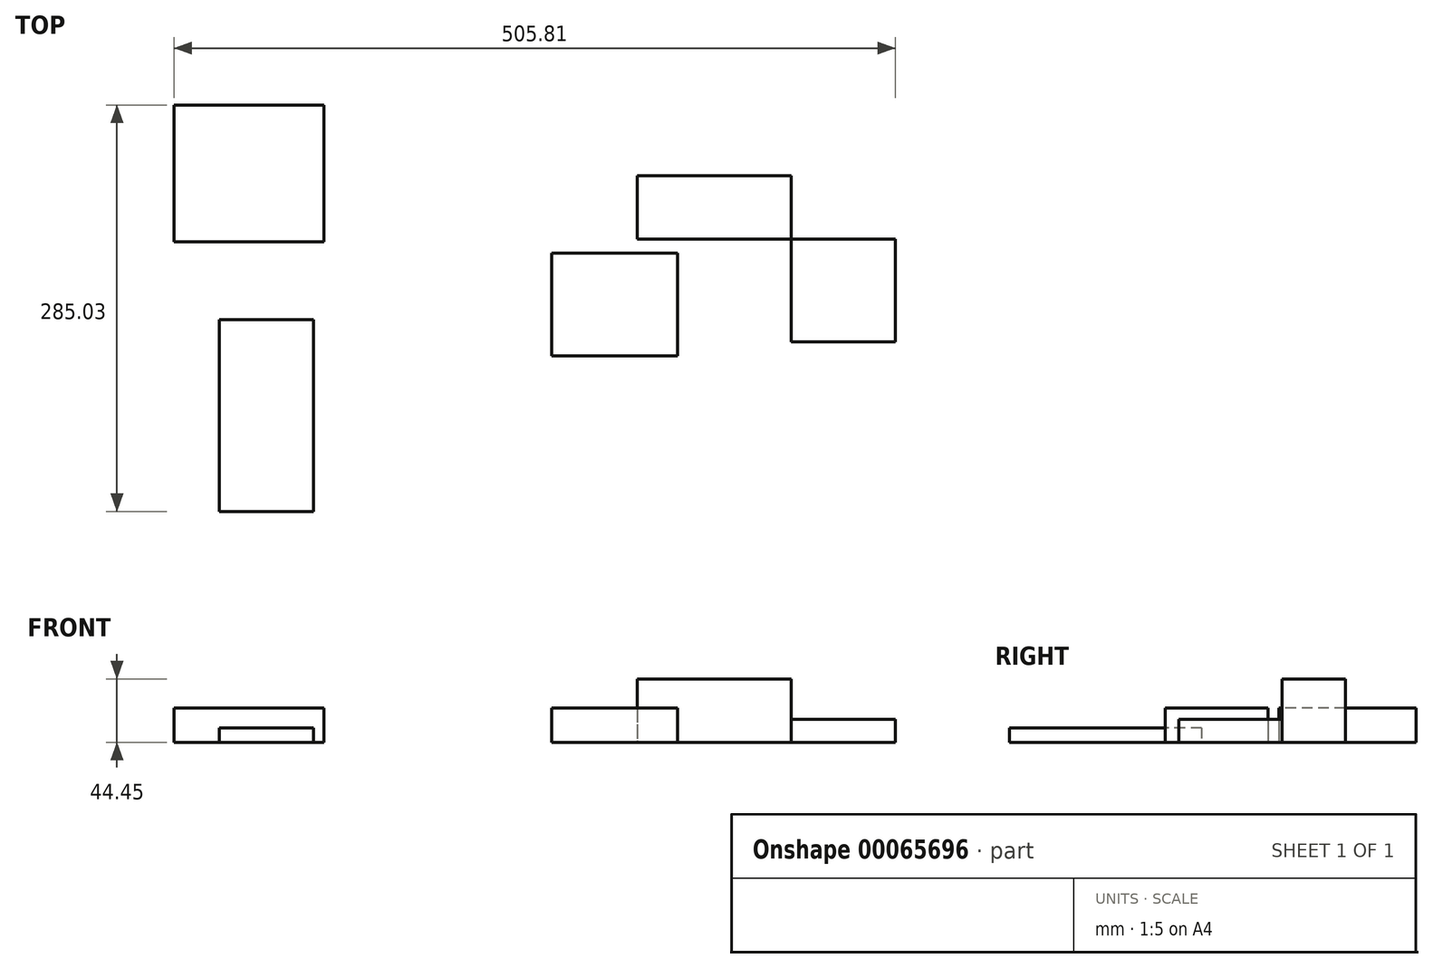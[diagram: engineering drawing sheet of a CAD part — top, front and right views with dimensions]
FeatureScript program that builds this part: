
annotation { "Feature Type Name" : "Feature", "Feature Type Description" : "" }
export const myFeature = defineFeature(function(context is Context, id is Id, definition is map)
    precondition{}
    {
        {
            var Q0;
            Q0=qCreatedBy(makeId("Top.planeOp"),FACE);
            var sketch = newSketch(context, id + "F0", { "sketchPlane" : qUnion([Q0])});
            skLineSegment(sketch, "E0.bottom", {"start": v(-107.95, 44.45) * mm, "end": v(0, 44.45) * mm});
            skLineSegment(sketch, "E0.top", {"start": v(-107.95, 0) * mm, "end": v(0, 0) * mm});
            skLineSegment(sketch, "E0.left", {"start": v(-107.95, 44.45) * mm, "end": v(-107.95, 0) * mm});
            skLineSegment(sketch, "E0.right", {"start": v(0, 44.45) * mm, "end": v(0, 0) * mm});
            skSolve(sketch);
        }
        {
            var Q0;
            Q0=makeQuery(id+"F0.imprint","IMPRINT",FACE,{"disambiguationData":[TD([[makeQuery(id+"F0.imprint","IMPRINT",EDGE,{"derivedFrom":sQuery(id+"F0.wireOp",EDGE,"E0.bottom")}),-1.0]])]});
            extrude(context, id + "F1", {"entities" : qUnion([Q0]), "depth" : 44.45 * mm});
        }
        {
            var Q0;
            Q0=qCreatedBy(makeId("Top.planeOp"),FACE);
            var sketch = newSketch(context, id + "F2", { "sketchPlane" : qUnion([Q0])});
            skLineSegment(sketch, "E1.bottom", {"start": v(0, 0) * mm, "end": v(73.15, 0) * mm});
            skLineSegment(sketch, "E1.top", {"start": v(0, -72.14) * mm, "end": v(73.15, -72.14) * mm});
            skLineSegment(sketch, "E1.left", {"start": v(0, 0) * mm, "end": v(0, -72.14) * mm});
            skLineSegment(sketch, "E1.right", {"start": v(73.15, 0) * mm, "end": v(73.15, -72.14) * mm});
            skSolve(sketch);
        }
        {
            var Q0;
            Q0=makeQuery(id+"F2.imprint","IMPRINT",FACE,{"disambiguationData":[TD([[makeQuery(id+"F2.imprint","IMPRINT",EDGE,{"derivedFrom":sQuery(id+"F2.wireOp",EDGE,"E1.bottom")}),-1.0]])]});
            extrude(context, id + "F3", {"entities" : qUnion([Q0]), "depth" : 16.26 * mm});
        }
        {
            var Q0;
            Q0=qCreatedBy(makeId("Top.planeOp"),FACE);
            var sketch = newSketch(context, id + "F4", { "sketchPlane" : qUnion([Q0])});
            skLineSegment(sketch, "E2.bottom", {"start": v(-167.83, -9.68) * mm, "end": v(-79.69, -9.68) * mm});
            skLineSegment(sketch, "E2.top", {"start": v(-167.83, -81.82) * mm, "end": v(-79.69, -81.82) * mm});
            skLineSegment(sketch, "E2.left", {"start": v(-167.83, -9.68) * mm, "end": v(-167.83, -81.82) * mm});
            skLineSegment(sketch, "E2.right", {"start": v(-79.69, -9.68) * mm, "end": v(-79.69, -81.82) * mm});
            skSolve(sketch);
        }
        {
            var Q0;
            Q0=qSketchRegion(id+"F4",true);
            extrude(context, id + "F5", {"entities" : qUnion([Q0]), "depth" : 24.13 * mm});
        }
        {
            var Q0;
            Q0=qCreatedBy(makeId("Top.planeOp"),FACE);
            var sketch = newSketch(context, id + "F6", { "sketchPlane" : qUnion([Q0])});
            skLineSegment(sketch, "E3.bottom", {"start": v(-432.66, 94.04) * mm, "end": v(-327.5, 94.04) * mm});
            skLineSegment(sketch, "E3.top", {"start": v(-432.66, -1.97) * mm, "end": v(-327.5, -1.97) * mm});
            skLineSegment(sketch, "E3.left", {"start": v(-432.66, 94.04) * mm, "end": v(-432.66, -1.97) * mm});
            skLineSegment(sketch, "E3.right", {"start": v(-327.5, 94.04) * mm, "end": v(-327.5, -1.97) * mm});
            skSolve(sketch);
        }
        {
            var Q0;
            Q0=makeQuery(id+"F6.imprint","IMPRINT",FACE,{"disambiguationData":[TD([[makeQuery(id+"F6.imprint","IMPRINT",EDGE,{"derivedFrom":sQuery(id+"F6.wireOp",EDGE,"E3.bottom")}),-1.0]])]});
            extrude(context, id + "F7", {"entities" : qUnion([Q0]), "depth" : 24.13 * mm});
        }
        {
            var Q0;
            Q0=qCreatedBy(makeId("Top.planeOp"),FACE);
            var sketch = newSketch(context, id + "F8", { "sketchPlane" : qUnion([Q0])});
            skLineSegment(sketch, "E4.bottom", {"start": v(-401.06, -56.37) * mm, "end": v(-335.02, -56.37) * mm});
            skLineSegment(sketch, "E4.top", {"start": v(-401.06, -191) * mm, "end": v(-335.02, -191) * mm});
            skLineSegment(sketch, "E4.left", {"start": v(-401.06, -56.37) * mm, "end": v(-401.06, -191) * mm});
            skLineSegment(sketch, "E4.right", {"start": v(-335.02, -56.37) * mm, "end": v(-335.02, -191) * mm});
            skSolve(sketch);
        }
        {
            var Q0;
            Q0=qSketchRegion(id+"F8",true);
            extrude(context, id + "F9", {"entities" : qUnion([Q0]), "depth" : 10.16 * mm});
        }
    });
